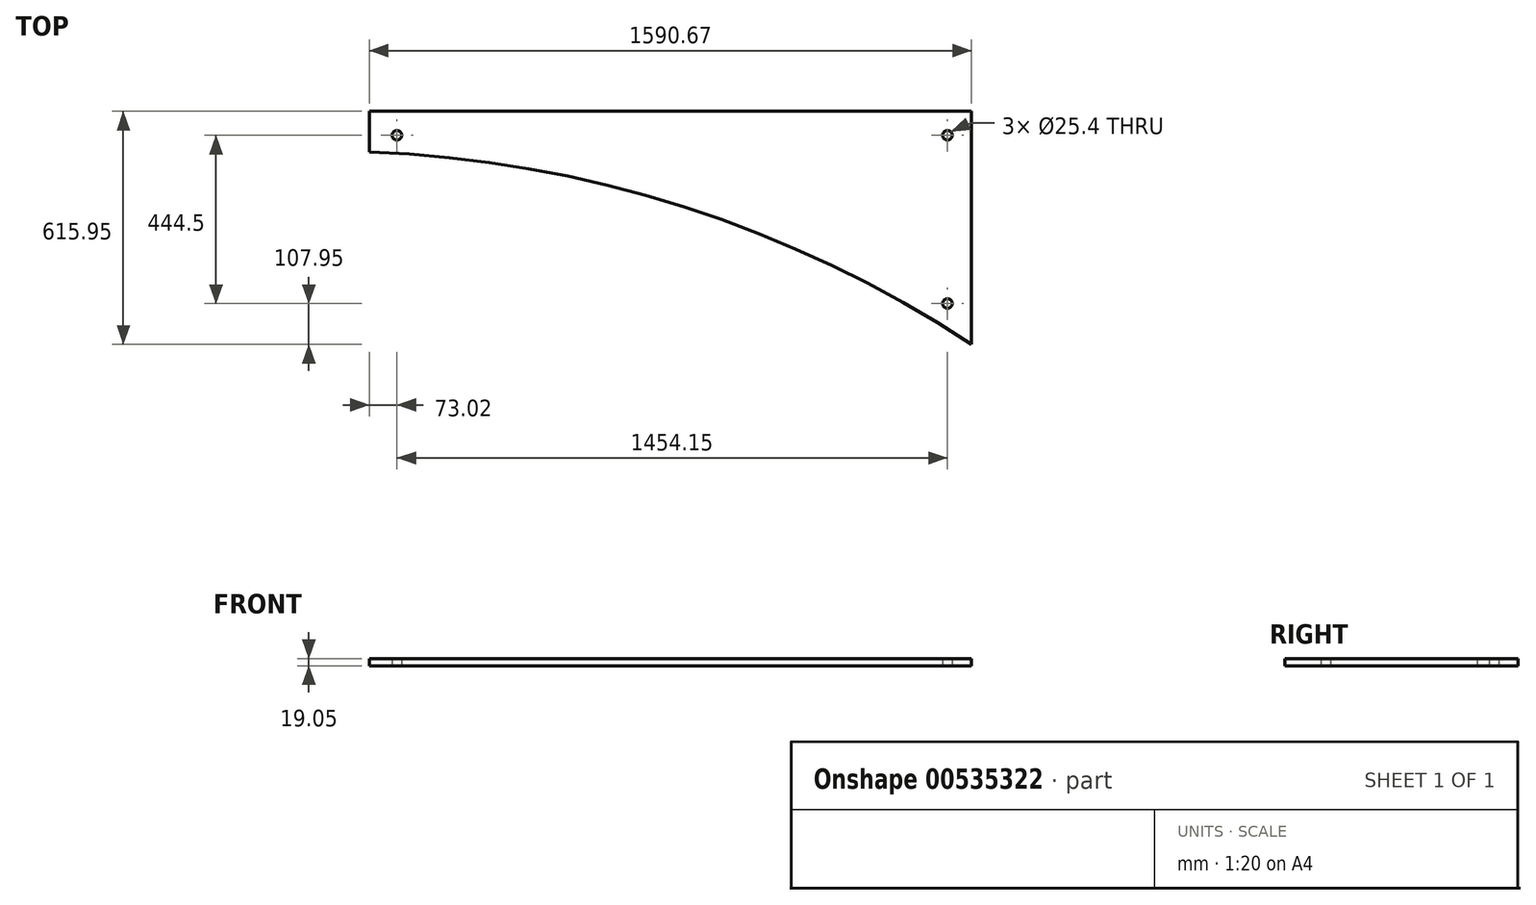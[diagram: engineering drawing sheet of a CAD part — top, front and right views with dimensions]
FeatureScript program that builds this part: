
annotation { "Feature Type Name" : "Feature", "Feature Type Description" : "" }
export const myFeature = defineFeature(function(context is Context, id is Id, definition is map)
    precondition{}
    {
        {
            var Q0;
            Q0=qCreatedBy(makeId("Top.planeOp"),FACE);
            var sketch = newSketch(context, id + "F0", { "sketchPlane" : qUnion([Q0])});
            skLineSegment(sketch, "E0", {"start": v(0, 0) * mm, "end": v(0, 615.95) * mm});
            skLineSegment(sketch, "E1", {"start": v(0, 615.95) * mm, "end": v(0, 615.95) * mm});
            skLineSegment(sketch, "E2", {"start": v(0, 615.95) * mm, "end": v(-1590.67, 615.95) * mm});
            skLineSegment(sketch, "E3", {"start": v(-795.34, 615.95) * mm, "end": v(-795.34, 374.65) * mm, "construction": true});
            skLineSegment(sketch, "E4", {"start": v(-1590.67, 615.95) * mm, "end": v(-1590.67, 508) * mm});
            skArc(sketch, "E5", {"start": v(0, 0) * mm, "mid": v(-760.3, 363.7) * mm, "end": v(-1590.68, 508) * mm});
            skLineSegment(sketch, "E6.0", {"start": v(-63.5, 552.45) * mm, "end": v(-1590.67, 552.45) * mm, "construction": true});
            skCircle(sketch, "E7", {"center": v(-63.5, 552.45) * mm, "radius": 12.7 * mm});
            skLineSegment(sketch, "E8.0", {"start": v(0, 107.95) * mm, "end": v(-63.5, 107.95) * mm, "construction": true});
            skLineSegment(sketch, "E9.trimOffspring", {"start": v(-63.5, 107.95) * mm, "end": v(-63.5, 552.45) * mm, "construction": true});
            skCircle(sketch, "E10", {"center": v(-63.5, 107.95) * mm, "radius": 12.7 * mm});
            skLineSegment(sketch, "E11.0", {"start": v(-1517.65, 552.45) * mm, "end": v(-1517.65, 615.95) * mm, "construction": true});
            skCircle(sketch, "E12", {"center": v(-1517.65, 552.45) * mm, "radius": 12.7 * mm});
            skSolve(sketch);
        }
        {
            var Q0;
            Q0=makeQuery(id+"F0.imprint","IMPRINT",FACE,{"disambiguationData":[TD([[makeQuery(id+"F0.imprint","IMPRINT",EDGE,{"derivedFrom":sQuery(id+"F0.wireOp",EDGE,"E0")}),1.0]])]});
            extrude(context, id + "F1", {"entities" : qUnion([Q0]), "depth" : 19.05 * mm, "offsetDistance" : 25.4 * mm});
        }
    });
